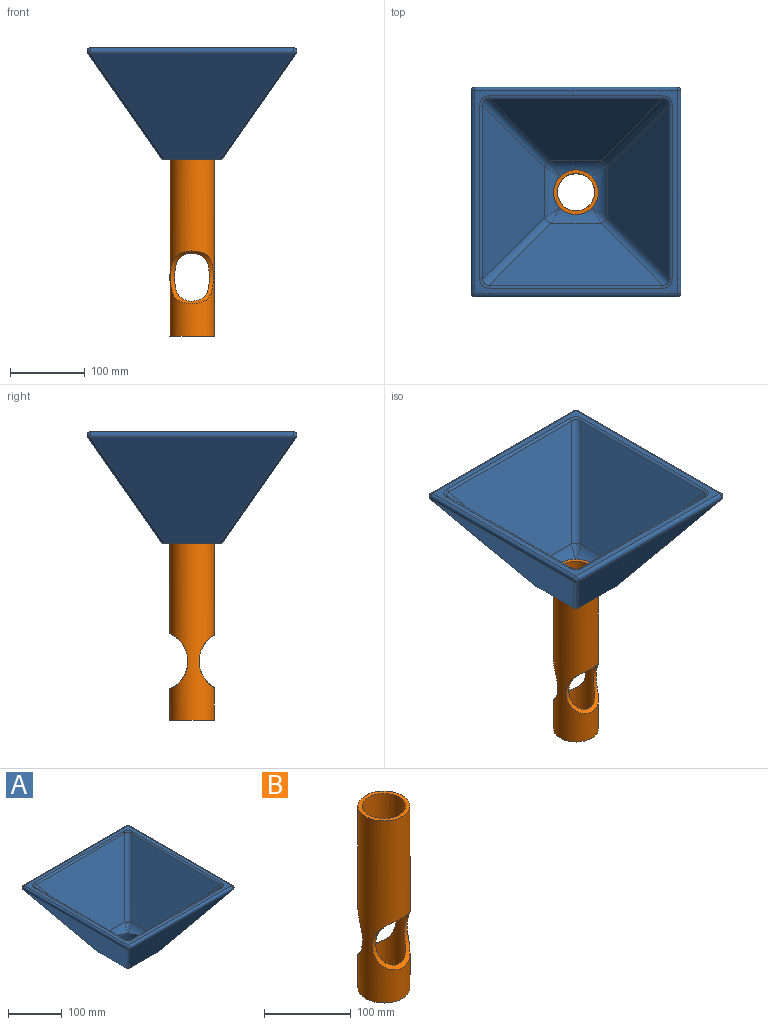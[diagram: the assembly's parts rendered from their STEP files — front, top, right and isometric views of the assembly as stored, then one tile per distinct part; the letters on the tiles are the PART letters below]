
ASSEMBLY  parts=2 mates=1
PART A: 47 faces, bbox 280.9x280.9x150.7 mm
  f0: plane 0.15x0.15mm, normal (0,0,1), area 0mm2, adj f14,f16,f26
  f1: plane 0.15x0.15mm, normal (0,0,1), area 0mm2, adj f14,f15,f26
  f2: plane 0.15x0.15mm, normal (0,0,1), area 0mm2, adj f15,f17,f26
  f3: plane 270.85x270.85mm, normal (0,0,1), area 7291.8mm2, adj f27,f28,f29,f30,f31,f32,f33,f34
  f4: plane 270.85x142.13mm, normal (0.82,0,-0.57), area 29727.8mm2, adj f8,f37,f43,f46
  f5: plane 270.85x142.13mm, normal (0,0.82,-0.57), area 29727.8mm2, adj f8,f40,f44,f46
  f6: plane 270.85x142.13mm, normal (-0.82,0,-0.57), area 29727.8mm2, adj f8,f35,f39,f40
  f7: plane 270.85x142.13mm, normal (0,-0.82,-0.57), area 29727.8mm2, adj f8,f35,f37,f38
  f8: plane 80x80mm, normal (0,0,-1), area 3559.5mm2, adj f4,f5,f6,f7,f26,f35,f37,f40
  f9: plane 232.69x118.21mm, normal (0,-0.82,0.57), area 21634.7mm2, adj f14,f19,f21,f28
  f10: plane 232.69x118.21mm, normal (0.82,0,0.57), area 21634.7mm2, adj f15,f21,f23,f29
  f11: plane 232.69x118.21mm, normal (0,0.82,0.57), area 21634.7mm2, adj f17,f23,f25,f33
  f12: plane 232.69x118.21mm, normal (-0.82,0,0.57), area 21634.7mm2, adj f16,f19,f25,f32
  f13: plane 0.15x0.15mm, normal (0,0,1), area 0mm2, adj f16,f17,f26
  f14: cylinder r=25mm len=67.15mm, axis (1,0,0), area 1084.3mm2, adj f0,f1,f9,f18,f20,f26
  f15: cylinder r=25mm len=67.15mm, axis (0,-1,0), area 1084.3mm2, adj f1,f2,f10,f20,f22,f26
  f16: cylinder r=25mm len=67.15mm, axis (0,-1,0), area 1084.3mm2, adj f0,f12,f13,f18,f24,f26
  f17: cylinder r=25mm len=67.15mm, axis (1,0,0), area 1084.3mm2, adj f2,f11,f13,f22,f24,f26
  f18: bspline ~21.24x21.24mm, area 172.2mm2, adj f14,f16,f19
  f19: cylinder r=10mm len=121.46mm, axis (-0.5,-0.5,-0.71), area 2077.9mm2, adj f9,f12,f18,f30
  f20: bspline ~21.24x21.24mm, area 172.2mm2, adj f14,f15,f21
  f21: cylinder r=10mm len=121.46mm, axis (0.5,-0.5,-0.71), area 2077.9mm2, adj f9,f10,f20,f27
  f22: bspline ~21.24x21.24mm, area 172.2mm2, adj f15,f17,f23
  f23: cylinder r=10mm len=121.46mm, axis (0.5,0.5,-0.71), area 2077.9mm2, adj f10,f11,f22,f31
  f24: bspline ~21.24x21.24mm, area 172.2mm2, adj f16,f17,f25
  f25: cylinder r=10mm len=121.46mm, axis (-0.5,0.5,-0.71), area 2077.9mm2, adj f11,f12,f24,f34
  f26: cylinder r=30mm len=60mm, axis (0,0,1), area 3734.7mm2, adj f0,f1,f2,f8,f13,f14,f15,f16
  f27: bspline ~12.29x12.29mm, area 70mm2, adj f3,f21,f28,f29
  f28: cylinder r=5mm len=232.69mm, axis (-1,0,0), area 1116.8mm2, adj f3,f9,f27,f30
  f29: cylinder r=5mm len=232.69mm, axis (0,1,0), area 1116.8mm2, adj f3,f10,f27,f31
  f30: bspline ~12.29x12.29mm, area 70mm2, adj f3,f19,f28,f32
  f31: bspline ~12.29x12.29mm, area 70mm2, adj f3,f23,f29,f33
  f32: cylinder r=5mm len=232.69mm, axis (0,1,0), area 1116.8mm2, adj f3,f12,f30,f34
  f33: cylinder r=5mm len=232.69mm, axis (-1,0,0), area 1116.8mm2, adj f3,f11,f31,f34
  f34: bspline ~12.29x12.29mm, area 70mm2, adj f3,f25,f32,f33
  f35: cylinder r=5mm len=142.78mm, axis (0.5,0.5,-0.71), area 1232mm2, adj f6,f7,f8,f36
  f36: sphere r=5mm, area 65.3mm2, adj f35,f38,f39
  f37: cylinder r=5mm len=142.78mm, axis (-0.5,0.5,-0.71), area 1232mm2, adj f4,f7,f8,f41
  f38: cylinder r=5mm len=270.85mm, axis (-1,0,0), area 2954.5mm2, adj f3,f7,f36,f41
  f39: cylinder r=5mm len=270.85mm, axis (0,-1,0), area 2954.5mm2, adj f3,f6,f36,f42
  f40: cylinder r=5mm len=142.78mm, axis (0.5,-0.5,-0.71), area 1232mm2, adj f5,f6,f8,f42
  f41: sphere r=5mm, area 65.3mm2, adj f37,f38,f43
  f42: sphere r=5mm, area 65.3mm2, adj f39,f40,f44
  f43: cylinder r=5mm len=270.85mm, axis (0,-1,0), area 2954.5mm2, adj f3,f4,f41,f45
  f44: cylinder r=5mm len=270.85mm, axis (-1,0,0), area 2954.5mm2, adj f3,f5,f42,f45
  f45: sphere r=5mm, area 65.3mm2, adj f43,f44,f46
  f46: cylinder r=5mm len=142.78mm, axis (-0.5,-0.5,-0.71), area 1232mm2, adj f4,f5,f8,f45
PART B: 6 faces, bbox 60x60x257 mm
  f0: cylinder r=30mm len=257mm, axis (0,0,-1), area 39182.1mm2, adj f1,f2,f4,f5
  f1: plane 60x60mm, normal (0,0,1), area 863.9mm2, adj f0,f3
  f2: plane 60x60mm, normal (0,0,-1), area 863.9mm2, adj f0,f3
  f3: cylinder r=25mm len=257mm, axis (0,0,-1), area 33636.3mm2, adj f1,f2,f4,f5
  f4: cylinder r=40.5mm len=74.41mm, axis (1,0,0), area 1276.3mm2, adj f0,f3
  f5: cylinder r=40.5mm len=70.44mm, axis (1,0,0), area 1223.7mm2, adj f0,f3
PLACE A t=(-74.51,48.31,26.26)mm
PLACE B t=(-114.51,8.31,-209.99)mm
MATE fastened A.f26 <-> B.f3  axis (0,0,1) through (-114.51,8.31,47.01)mm
